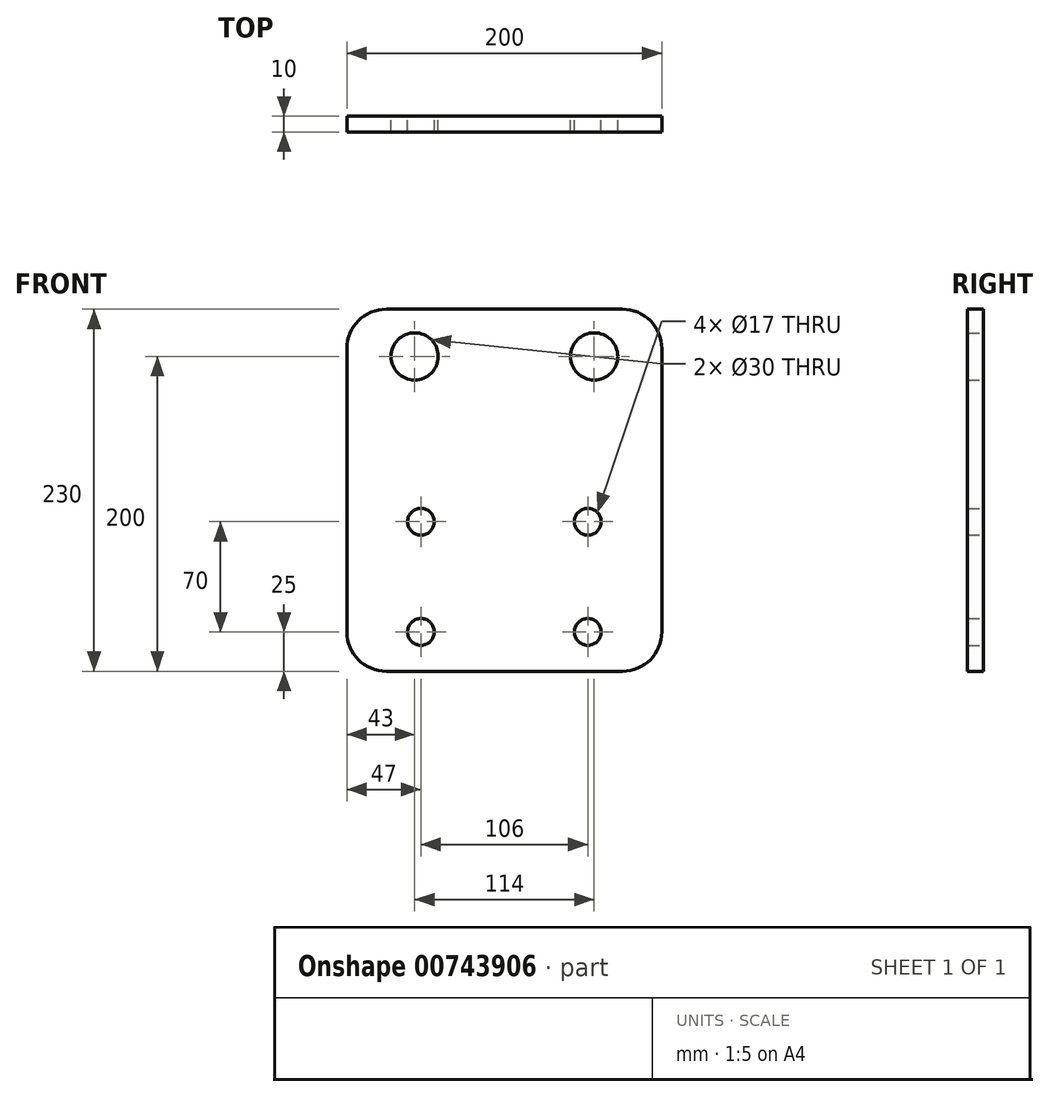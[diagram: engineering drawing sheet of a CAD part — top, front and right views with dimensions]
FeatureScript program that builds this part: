
annotation { "Feature Type Name" : "Feature", "Feature Type Description" : "" }
export const myFeature = defineFeature(function(context is Context, id is Id, definition is map)
    precondition{}
    {
        {
            var Q0;
            Q0=qCreatedBy(makeId("Front.planeOp"),FACE);
            var sketch = newSketch(context, id + "F0", { "sketchPlane" : qUnion([Q0])});
            skLineSegment(sketch, "E0.bottom", {"start": v(25, 0) * mm, "end": v(175, 0) * mm});
            skLineSegment(sketch, "E0.top", {"start": v(25, 230) * mm, "end": v(175, 230) * mm});
            skLineSegment(sketch, "E0.left", {"start": v(0, 25) * mm, "end": v(0, 205) * mm});
            skLineSegment(sketch, "E0.right", {"start": v(200, 25) * mm, "end": v(200, 205) * mm});
            skCircle(sketch, "E1", {"center": v(43, 200) * mm, "radius": 15 * mm});
            skCircle(sketch, "E2", {"center": v(157, 200) * mm, "radius": 15 * mm});
            skCircle(sketch, "E3", {"center": v(47, 95) * mm, "radius": 8.5 * mm});
            skCircle(sketch, "E4", {"center": v(153, 95) * mm, "radius": 8.5 * mm});
            skCircle(sketch, "E5", {"center": v(153, 25) * mm, "radius": 8.5 * mm});
            skCircle(sketch, "E6", {"center": v(47, 25) * mm, "radius": 8.5 * mm});
            skPoint(sketch, "E7.visualSharp", {"position": v(0, 230) * mm});
            skArc(sketch, "E7.filletArc", {"start": v(25, 230) * mm, "mid": v(7.32, 222.68) * mm, "end": v(0, 205) * mm});
            skPoint(sketch, "E8.visualSharp", {"position": v(200, 230) * mm});
            skArc(sketch, "E8.filletArc", {"start": v(200, 205) * mm, "mid": v(192.68, 222.68) * mm, "end": v(175, 230) * mm});
            skPoint(sketch, "E9.visualSharp", {"position": v(200, 0) * mm});
            skArc(sketch, "E9.filletArc", {"start": v(175, 0) * mm, "mid": v(192.68, 7.32) * mm, "end": v(200, 25) * mm});
            skPoint(sketch, "E10.visualSharp", {"position": v(0, 0) * mm});
            skArc(sketch, "E10.filletArc", {"start": v(0, 25) * mm, "mid": v(7.32, 7.32) * mm, "end": v(25, 0) * mm});
            skSolve(sketch);
        }
        {
            var Q0;
            Q0=makeQuery(id+"F0.imprint","IMPRINT",FACE,{"disambiguationData":[TD([[makeQuery(id+"F0.imprint","IMPRINT",EDGE,{"derivedFrom":sQuery(id+"F0.wireOp",EDGE,"E0.bottom")}),1.0]])]});
            extrude(context, id + "F1", {"entities" : qUnion([Q0]), "depth" : 10 * mm, "offsetDistance" : 25 * mm});
        }
    });
